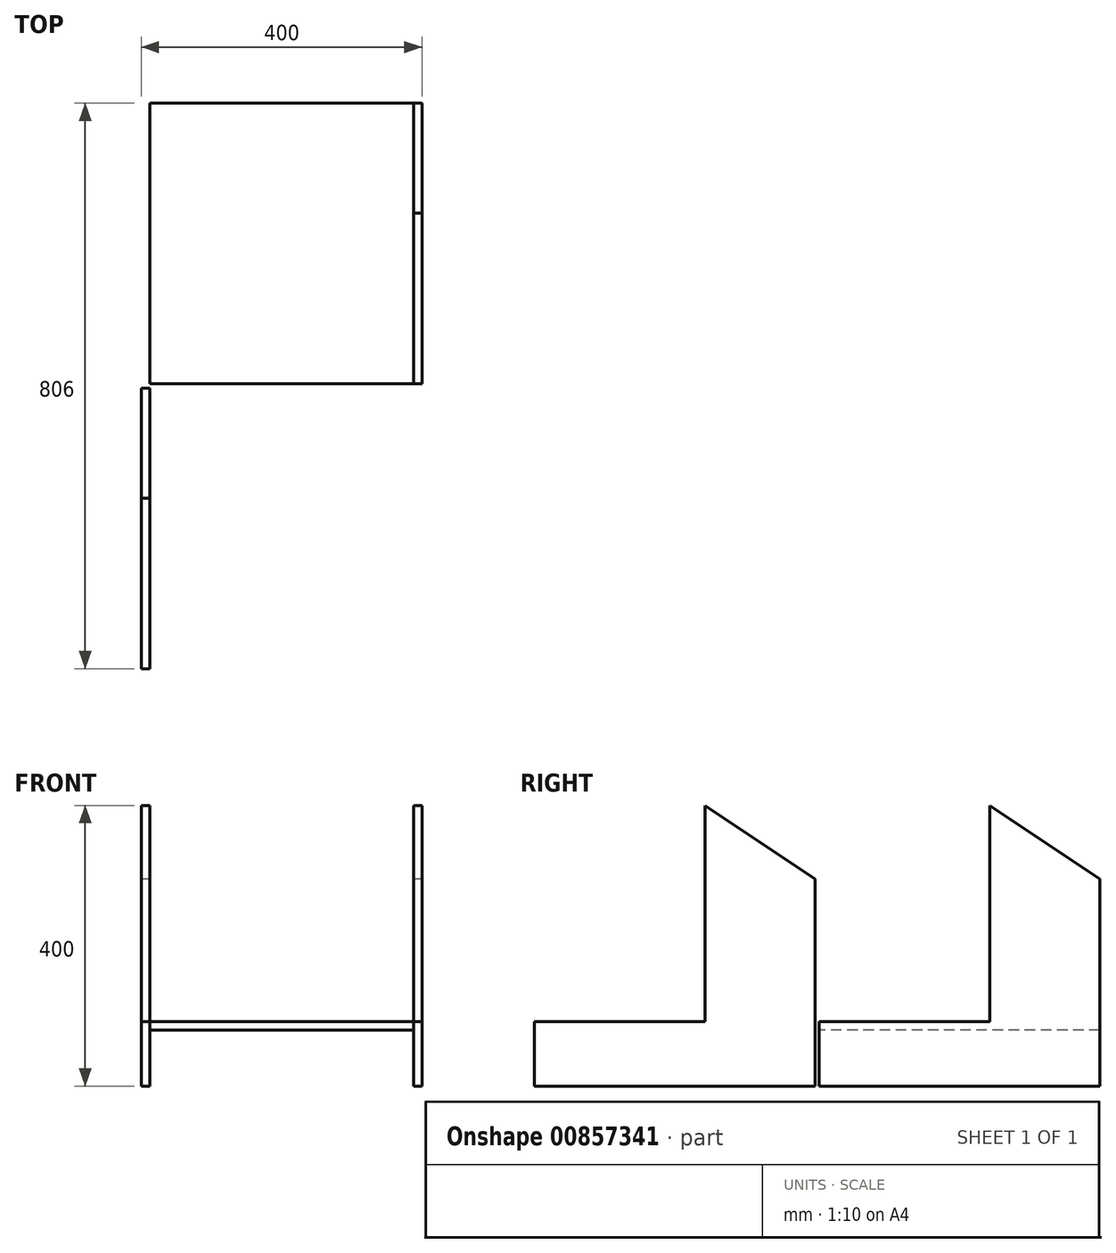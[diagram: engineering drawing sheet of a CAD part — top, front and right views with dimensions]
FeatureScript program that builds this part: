
annotation { "Feature Type Name" : "Feature", "Feature Type Description" : "" }
export const myFeature = defineFeature(function(context is Context, id is Id, definition is map)
    precondition{}
    {
        {
            var Q0;
            Q0=qCreatedBy(makeId("Top.planeOp"),FACE);
            var sketch = newSketch(context, id + "F0", { "sketchPlane" : qUnion([Q0])});
            skLineSegment(sketch, "E0.bottom", {"start": v(188, 200) * mm, "end": v(-188, 200) * mm});
            skLineSegment(sketch, "E0.top", {"start": v(188, -200) * mm, "end": v(-188, -200) * mm});
            skLineSegment(sketch, "E0.left", {"start": v(188, 200) * mm, "end": v(188, -200) * mm});
            skLineSegment(sketch, "E0.right", {"start": v(-188, 200) * mm, "end": v(-188, -200) * mm});
            skPoint(sketch, "E0.middle", {"position": v(0, 0) * mm});
            skSolve(sketch);
        }
        {
            var Q0;
            Q0=makeQuery(id+"F0.imprint","IMPRINT",FACE,{"disambiguationData":[TD([[makeQuery(id+"F0.imprint","IMPRINT",EDGE,{"derivedFrom":sQuery(id+"F0.wireOp",EDGE,"E0.bottom")}),1.0]])]});
            extrude(context, id + "F1", {"entities" : qUnion([Q0]), "depth" : 12 * mm, "offsetDistance" : 25 * mm});
        }
        {
            var Q0;
            Q0=makeQuery(id+"F1.opExtrude","SWEPT_FACE",FACE,{"disambiguationData":[OSD([sQuery(id+"F0.wireOp",EDGE,"E0.left")])]});
            var sketch = newSketch(context, id + "F2", { "sketchPlane" : qUnion([Q0])});
            skLineSegment(sketch, "E1.bottom", {"start": v(-200, 12) * mm, "end": v(200, 12) * mm});
            skLineSegment(sketch, "E1.top", {"start": v(-200, -80) * mm, "end": v(200, -80) * mm});
            skLineSegment(sketch, "E1.left", {"start": v(-200, 12) * mm, "end": v(-200, -80) * mm});
            skLineSegment(sketch, "E1.right", {"start": v(200, 12) * mm, "end": v(200, -80) * mm});
            skLineSegment(sketch, "E2", {"start": v(43.23, 12) * mm, "end": v(43.23, 320) * mm});
            skLineSegment(sketch, "E3", {"start": v(200, 12) * mm, "end": v(200, 215.31) * mm});
            skFitSpline(sketch, "E4", {"points": [v(43.23, 320) * mm, v(200, 215.31) * mm], "startDerivative": vector(156.77, -104.69) * mm, "endDerivative": vector(156.77, -104.69) * mm});
            skFitSpline(sketch, "E5", {"points": [v(147.74, 250.2) * mm, v(163.96, 281.4) * mm], "startDerivative": vector(16.21, 31.19) * mm, "endDerivative": vector(16.21, 31.19) * mm});
            skSolve(sketch);
        }
        {
            var Q0;
            Q0 = qSketchRegion(id + "F2", true);
            var Q1;
            {var subQ0=sQuery(id+"F2.wireOp",EDGE,"E1.top");Q1=makeQuery(id+"F2.imprint","IMPRINT",FACE,{"disambiguationData":[TD([[makeQuery(id+"F2.imprint","IMPRINT",EDGE,{"derivedFrom":subQ0}),1.0]])]});}
            extrude(context, id + "F3", {"entities" : qUnion([Q0, Q1]), "depth" : 12 * mm, "offsetDistance" : 25 * mm});
        }
        {
            var Q0;
            Q0=makeQuery(id+"F3.opExtrude","SWEPT_BODY",BODY,{"disambiguationData":[OSD([sQuery(id+"F2.wireOp",EDGE,"E1.bottom"),sQuery(id+"F2.wireOp",EDGE,"E1.top"),sQuery(id+"F2.wireOp",EDGE,"E1.left"),sQuery(id+"F2.wireOp",EDGE,"E1.right"),sQuery(id+"F2.wireOp",EDGE,"E2"),sQuery(id+"F2.wireOp",EDGE,"E3"),sQuery(id+"F2.wireOp",EDGE,"E4")])]});
            transform(context, id + "F4", {"entities" : qUnion([Q0]), "transformType" : TransformType.TRANSLATION_3D, "dx" : -388 * mm, "dy" : -406 * mm, "dz" : 0 * mm, "makeCopy" : true});
        }
    });
